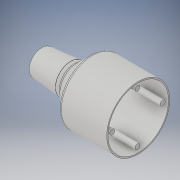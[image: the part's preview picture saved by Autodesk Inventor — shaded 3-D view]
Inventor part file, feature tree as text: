
AUTODESK INVENTOR PART (.ipt)
format: ipt  version: 2019 (Build 230136000, 136)  size: 232,960 bytes
history: native  units: mm
features: sketch x4, extrude x3, fillet x2, revolve x1, plane x1
ambient origin geometry x8: Origin, YZ Plane, XZ Plane, XY Plane, X Axis, Y Axis, Z Axis, Center Point
bodies: Solid1 (feature_tree)
feature tree (11):
  revolve  "Revolution1"  [1 undecoded]
  fillet  "Fillet1"  Radius=9.0mm
  fillet  "Fillet2"  Radius=22.0mm
  plane  "Work Plane1"
  extrude  "Extrusion1"  Depth=22.0mm
  extrude  "Extrusion2"  Depth=2.0mm
  extrude  "Extrusion3"  Depth=35.0mm
  sketch  "Sketch1"  dims[d0=20.0mm d1=0.872665mm d2=9.0mm d3=22.0mm]
  sketch  "Sketch2"  dims[d4=90.0deg d5=22.0mm]
  sketch  "Sketch3"  dims[d6=1.0mm d7=2.0mm]
  sketch  "Sketch4"  dims[d8=2.0mm d9=50.0mm d10=135.0deg d11=1.0mm d12=2.0mm d14=4.0mm d15=0.0mm d16=4.0mm d17=2.0mm d18=2.0mm d19=22.332156mm d21=4.0mm d22=0.0mm d24=2.0mm d25=8.0mm d26=0.0mm d28=4.0mm d29=4.0mm d30=4.0mm d31=20.0mm d32=20.0mm d33=20.0mm d34=20.0mm d35=35.0mm d36=0.0mm d37=36.0mm]
note: 1 required parameter value undecoded (feature->parameter linkage not recoverable at this tier; creation-order binding heuristic only, values carry confidence <= 0.55)
